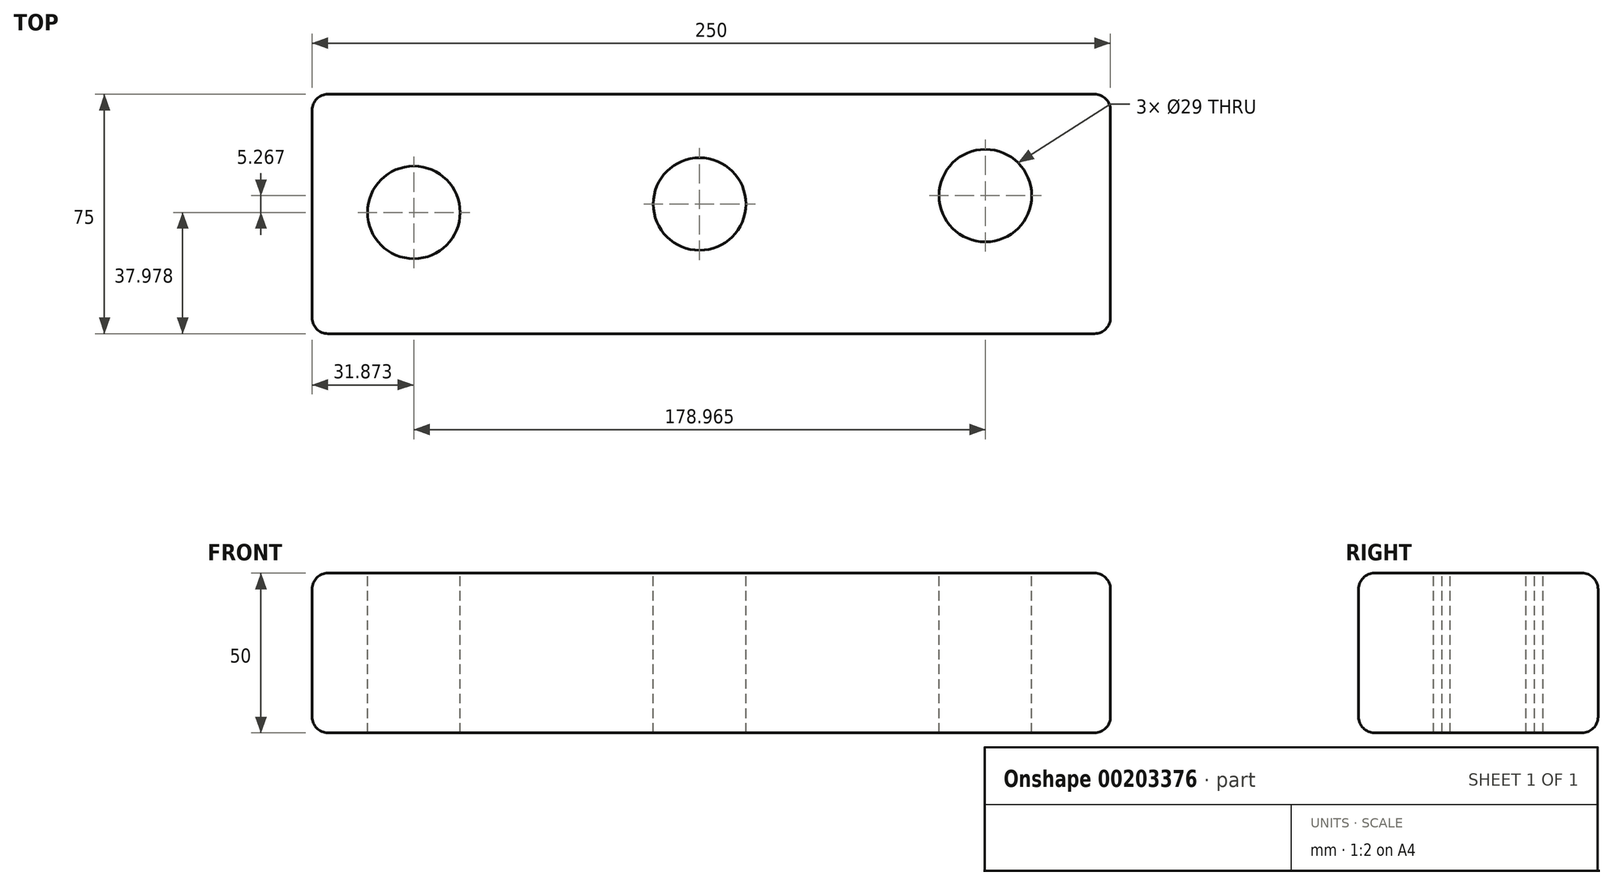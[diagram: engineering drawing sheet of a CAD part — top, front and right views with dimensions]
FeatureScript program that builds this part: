
annotation { "Feature Type Name" : "Feature", "Feature Type Description" : "" }
export const myFeature = defineFeature(function(context is Context, id is Id, definition is map)
    precondition{}
    {
        {
            var Q0;
            Q0=qCreatedBy(makeId("Top.planeOp"),FACE);
            var sketch = newSketch(context, id + "F0", { "sketchPlane" : qUnion([Q0])});
            skLineSegment(sketch, "E0.bottom", {"start": v(0, 0) * mm, "end": v(-250, 0) * mm});
            skLineSegment(sketch, "E0.top", {"start": v(0, 75) * mm, "end": v(-250, 75) * mm});
            skLineSegment(sketch, "E0.left", {"start": v(0, 0) * mm, "end": v(0, 75) * mm});
            skLineSegment(sketch, "E0.right", {"start": v(-250, 0) * mm, "end": v(-250, 75) * mm});
            skSolve(sketch);
        }
        {
            var Q0;
            Q0 = qSketchRegion(id + "F0", true);
            extrude(context, id + "F1", {"entities" : qUnion([Q0]), "endBound" : BoundingType.SYMMETRIC, "depth" : 50 * mm});
        }
        {
            var Q0;
            Q0=makeQuery(id+"F1.opExtrude","CAP_EDGE",EDGE,{"disambiguationData":[OSD([sQuery(id+"F0.wireOp",EDGE,"E0.left")])],"isStart":false});
            var Q1;
            Q1=makeQuery(id+"F1.opExtrude","SWEPT_EDGE",EDGE,{"disambiguationData":[OSD([sQuery(id+"F0.wireOp",EDGE,"E0.bottom"),sQuery(id+"F0.wireOp",EDGE,"E0.left")])]});
            var Q2;
            Q2=makeQuery(id+"F1.opExtrude","CAP_EDGE",EDGE,{"disambiguationData":[OSD([sQuery(id+"F0.wireOp",EDGE,"E0.left")])],"isStart":true});
            var Q3;
            Q3=makeQuery(id+"F1.opExtrude","SWEPT_EDGE",EDGE,{"disambiguationData":[OSD([sQuery(id+"F0.wireOp",EDGE,"E0.top"),sQuery(id+"F0.wireOp",EDGE,"E0.left")])]});
            var Q4;
            Q4=makeQuery(id+"F1.opExtrude","SWEPT_FACE",FACE,{"disambiguationData":[OSD([sQuery(id+"F0.wireOp",EDGE,"E0.bottom")])]});
            var Q5;
            Q5=makeQuery(id+"F1.opExtrude","CAP_EDGE",EDGE,{"disambiguationData":[OSD([sQuery(id+"F0.wireOp",EDGE,"E0.right")])],"isStart":false});
            var Q6;
            Q6=makeQuery(id+"F1.opExtrude","SWEPT_EDGE",EDGE,{"disambiguationData":[OSD([sQuery(id+"F0.wireOp",EDGE,"E0.top"),sQuery(id+"F0.wireOp",EDGE,"E0.right")])]});
            var Q7;
            Q7=makeQuery(id+"F1.opExtrude","CAP_EDGE",EDGE,{"disambiguationData":[OSD([sQuery(id+"F0.wireOp",EDGE,"E0.right")])],"isStart":true});
            var Q8;
            Q8=makeQuery(id+"F1.opExtrude","CAP_EDGE",EDGE,{"disambiguationData":[OSD([sQuery(id+"F0.wireOp",EDGE,"E0.top")])],"isStart":true});
            var Q9;
            Q9=makeQuery(id+"F1.opExtrude","CAP_EDGE",EDGE,{"disambiguationData":[OSD([sQuery(id+"F0.wireOp",EDGE,"E0.top")])],"isStart":false});
            fillet(context, id + "F2", {"entities" : qUnion([Q0, Q1, Q2, Q3, Q4, Q5, Q6, Q7, Q8, Q9]), "radius" : 5 * mm, "tangentPropagation" : true, "allowEdgeOverflow" : false});
        }
        {
            var Q0;
            Q0=makeQuery(id+"F1.opExtrude","CAP_FACE",FACE,{"disambiguationData":[OSD([sQuery(id+"F0.wireOp",EDGE,"E0.bottom"),sQuery(id+"F0.wireOp",EDGE,"E0.top"),sQuery(id+"F0.wireOp",EDGE,"E0.left"),sQuery(id+"F0.wireOp",EDGE,"E0.right")])],"isStart":false});
            var sketch = newSketch(context, id + "F3", { "sketchPlane" : qUnion([Q0])});
            skCircle(sketch, "E1", {"center": v(-218.13, 37.98) * mm, "radius": 14.5 * mm});
            skCircle(sketch, "E2", {"center": v(-128.64, 40.61) * mm, "radius": 14.5 * mm});
            skCircle(sketch, "E3", {"center": v(-39.16, 43.24) * mm, "radius": 14.5 * mm});
            skSolve(sketch);
        }
        {
            var Q0;
            Q0=sQuery(id+"F3.wireOp",VERTEX,"E2.center");
            var Q1;
            Q1=makeQuery(id+"F1.opExtrude","SWEPT_BODY",BODY,{"disambiguationData":[OSD([sQuery(id+"F0.wireOp",EDGE,"E0.bottom"),sQuery(id+"F0.wireOp",EDGE,"E0.top"),sQuery(id+"F0.wireOp",EDGE,"E0.left"),sQuery(id+"F0.wireOp",EDGE,"E0.right")])]});
            hole(context, id + "F4", {"style" : HoleStyle.SIMPLE, "endStyle" : HoleEndStyle.THROUGH, "holeDiameter" : 29 * mm, "locations" : qUnion([Q0]), "scope" : qUnion([Q1]), "isTappedThrough" : true});
        }
        {
            var Q0;
            Q0=sQuery(id+"F3.wireOp",VERTEX,"E3.center");
            var Q1;
            Q1=makeQuery(id+"F1.opExtrude","SWEPT_BODY",BODY,{"disambiguationData":[OSD([sQuery(id+"F0.wireOp",EDGE,"E0.bottom"),sQuery(id+"F0.wireOp",EDGE,"E0.top"),sQuery(id+"F0.wireOp",EDGE,"E0.left"),sQuery(id+"F0.wireOp",EDGE,"E0.right")])]});
            hole(context, id + "F5", {"style" : HoleStyle.SIMPLE, "endStyle" : HoleEndStyle.THROUGH, "holeDiameter" : 29 * mm, "locations" : qUnion([Q0]), "scope" : qUnion([Q1]), "isTappedThrough" : true});
        }
        {
            var Q0;
            Q0=sQuery(id+"F3.wireOp",VERTEX,"E1.center");
            var Q1;
            Q1=makeQuery(id+"F1.opExtrude","SWEPT_BODY",BODY,{"disambiguationData":[OSD([sQuery(id+"F0.wireOp",EDGE,"E0.bottom"),sQuery(id+"F0.wireOp",EDGE,"E0.top"),sQuery(id+"F0.wireOp",EDGE,"E0.left"),sQuery(id+"F0.wireOp",EDGE,"E0.right")])]});
            hole(context, id + "F6", {"style" : HoleStyle.SIMPLE, "endStyle" : HoleEndStyle.THROUGH, "holeDiameter" : 29 * mm, "locations" : qUnion([Q0]), "scope" : qUnion([Q1]), "isTappedThrough" : true});
        }
    });
